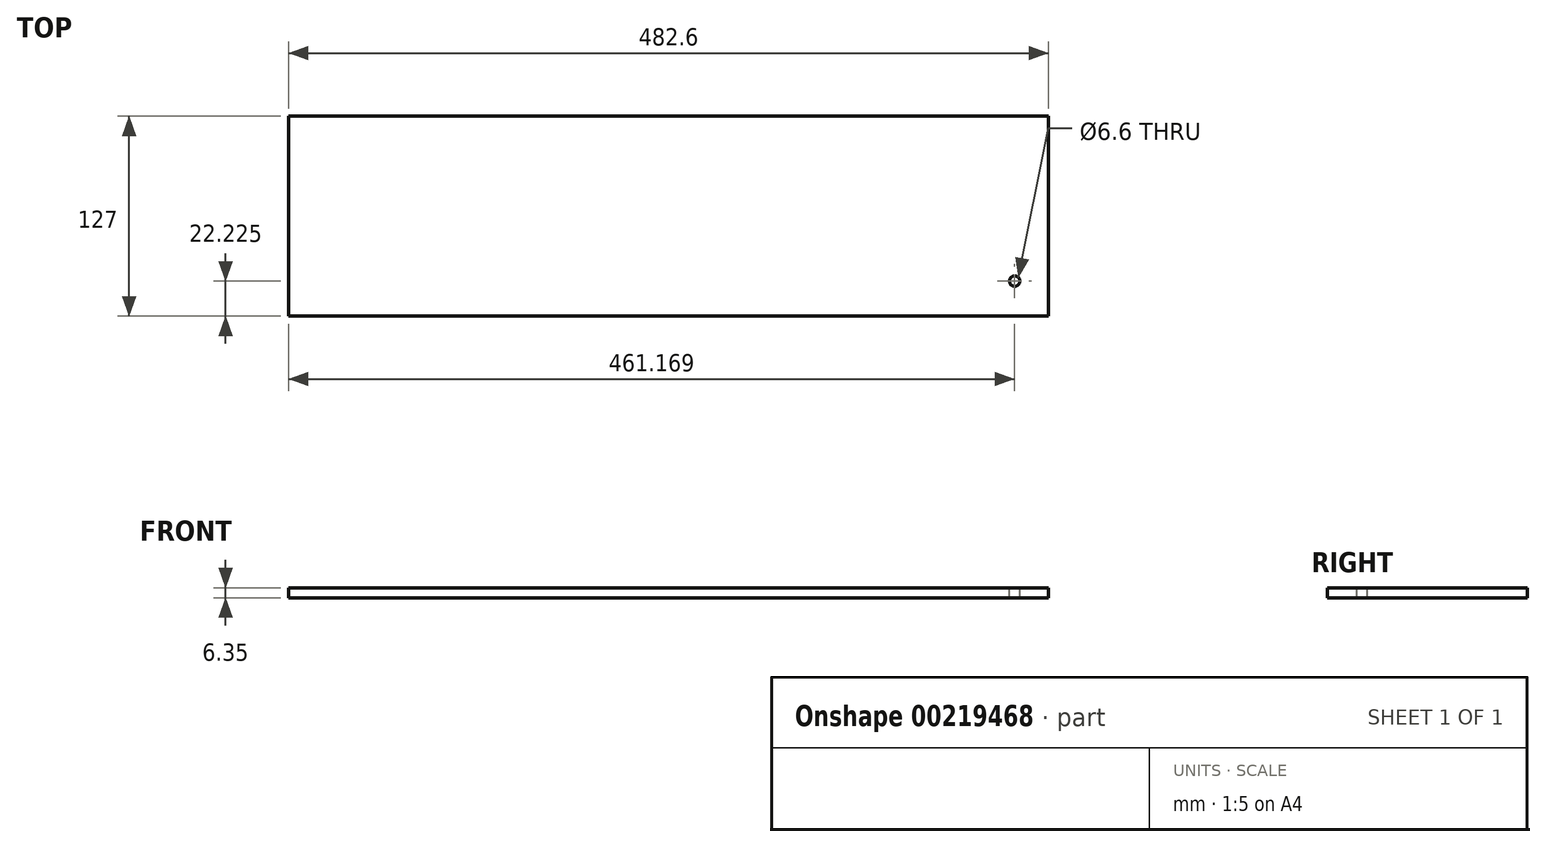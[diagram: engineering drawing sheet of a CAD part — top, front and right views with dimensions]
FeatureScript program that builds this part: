
annotation { "Feature Type Name" : "Feature", "Feature Type Description" : "" }
export const myFeature = defineFeature(function(context is Context, id is Id, definition is map)
    precondition{}
    {
        {
            var Q0;
            Q0=qCreatedBy(makeId("Top.planeOp"),FACE);
            var sketch = newSketch(context, id + "F0", { "sketchPlane" : qUnion([Q0])});
            skLineSegment(sketch, "E0.bottom", {"start": v(-241.3, -63.5) * mm, "end": v(241.3, -63.5) * mm});
            skLineSegment(sketch, "E0.top", {"start": v(-241.3, 63.5) * mm, "end": v(241.3, 63.5) * mm});
            skLineSegment(sketch, "E0.left", {"start": v(-241.3, -63.5) * mm, "end": v(-241.3, 63.5) * mm});
            skLineSegment(sketch, "E0.right", {"start": v(241.3, -63.5) * mm, "end": v(241.3, 63.5) * mm});
            skPoint(sketch, "E0.middle", {"position": v(0, 0) * mm});
            skSolve(sketch);
        }
        {
            var Q0;
            Q0=makeQuery(id+"F0.imprint","IMPRINT",FACE,{"disambiguationData":[TD([[makeQuery(id+"F0.imprint","IMPRINT",EDGE,{"derivedFrom":sQuery(id+"F0.wireOp",EDGE,"E0.bottom")}),1.0]])]});
            extrude(context, id + "F1", {"entities" : qUnion([Q0]), "oppositeDirection" : true, "depth" : 6.35 * mm});
        }
        {
            var Q0;
            Q0=makeQuery(id+"F1.opExtrude","CAP_FACE",FACE,{"disambiguationData":[OSD([sQuery(id+"F0.wireOp",EDGE,"E0.bottom"),sQuery(id+"F0.wireOp",EDGE,"E0.top"),sQuery(id+"F0.wireOp",EDGE,"E0.left"),sQuery(id+"F0.wireOp",EDGE,"E0.right")])],"isStart":true});
            var sketch = newSketch(context, id + "F2", { "sketchPlane" : qUnion([Q0])});
            skCircle(sketch, "E1", {"center": v(219.87, -41.28) * mm, "radius": 3.3 * mm});
            skSolve(sketch);
        }
        {
            var Q0;
            Q0=qSketchRegion(id+"F2",true);
            extrude(context, id + "F3", {"entities" : qUnion([Q0]), "operationType" : NewBodyOperationType.REMOVE, "oppositeDirection" : true, "depth" : 6.35 * mm});
        }
    });
